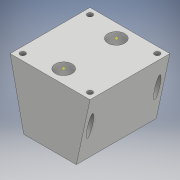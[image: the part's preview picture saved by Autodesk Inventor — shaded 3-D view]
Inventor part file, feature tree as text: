
AUTODESK INVENTOR PART (.ipt)
format: ipt  version: 2017 (Build 210142000, 142)  size: 140,288 bytes
history: native  units: mm
features: hole x3, sketch x3, extrude x2, other x2
ambient origin geometry x8: Origin, YZ Plane, XZ Plane, XY Plane, X Axis, Y Axis, Z Axis, Center Point
bodies: Solid1 (feature_tree)
feature tree (10):
  extrude  "Extrusion1"  Depth=38.0mm
  extrude  "Extrusion2"  Depth=4.2mm
  hole  "Hole1"  [1 undecoded]
  other  "Work Point1"
  other  "Work Point2"
  hole  "Hole2"  [1 undecoded]
  hole  "Hole3"  [1 undecoded]
  sketch  "Sketch1"  dims[d0=25.0mm d1=38.0mm]
  sketch  "Sketch2"  dims[d2=4.2mm d3=4.2mm]
  sketch  "Sketch3"  dims[d4=12.5mm d5=12.5mm d6=30.0mm d7=0.0mm d8=6.5mm d9=6.5mm d10=30.0mm d11=0.0mm d12=16.0mm d13=16.0mm d14=20.0mm d16=32.0mm d17=20.0mm d19=32.0mm d22=2.5mm d23=6.0mm d24=4.0mm d25=2.0mm d26=90.0deg d27=20.0mm d28=20.594885mm d29=10.0mm d30=10.0mm d31=8.0mm d32=6.0mm d33=4.0mm d34=2.0mm d35=90.0deg d36=26.0mm d37=20.594885mm d38=10.0mm d39=10.0mm d40=8.0mm d41=6.0mm d42=4.0mm d43=2.0mm d44=90.0deg d45=26.0mm d46=20.594885mm]
note: 3 required parameter values undecoded (feature->parameter linkage not recoverable at this tier; creation-order binding heuristic only, values carry confidence <= 0.55)
